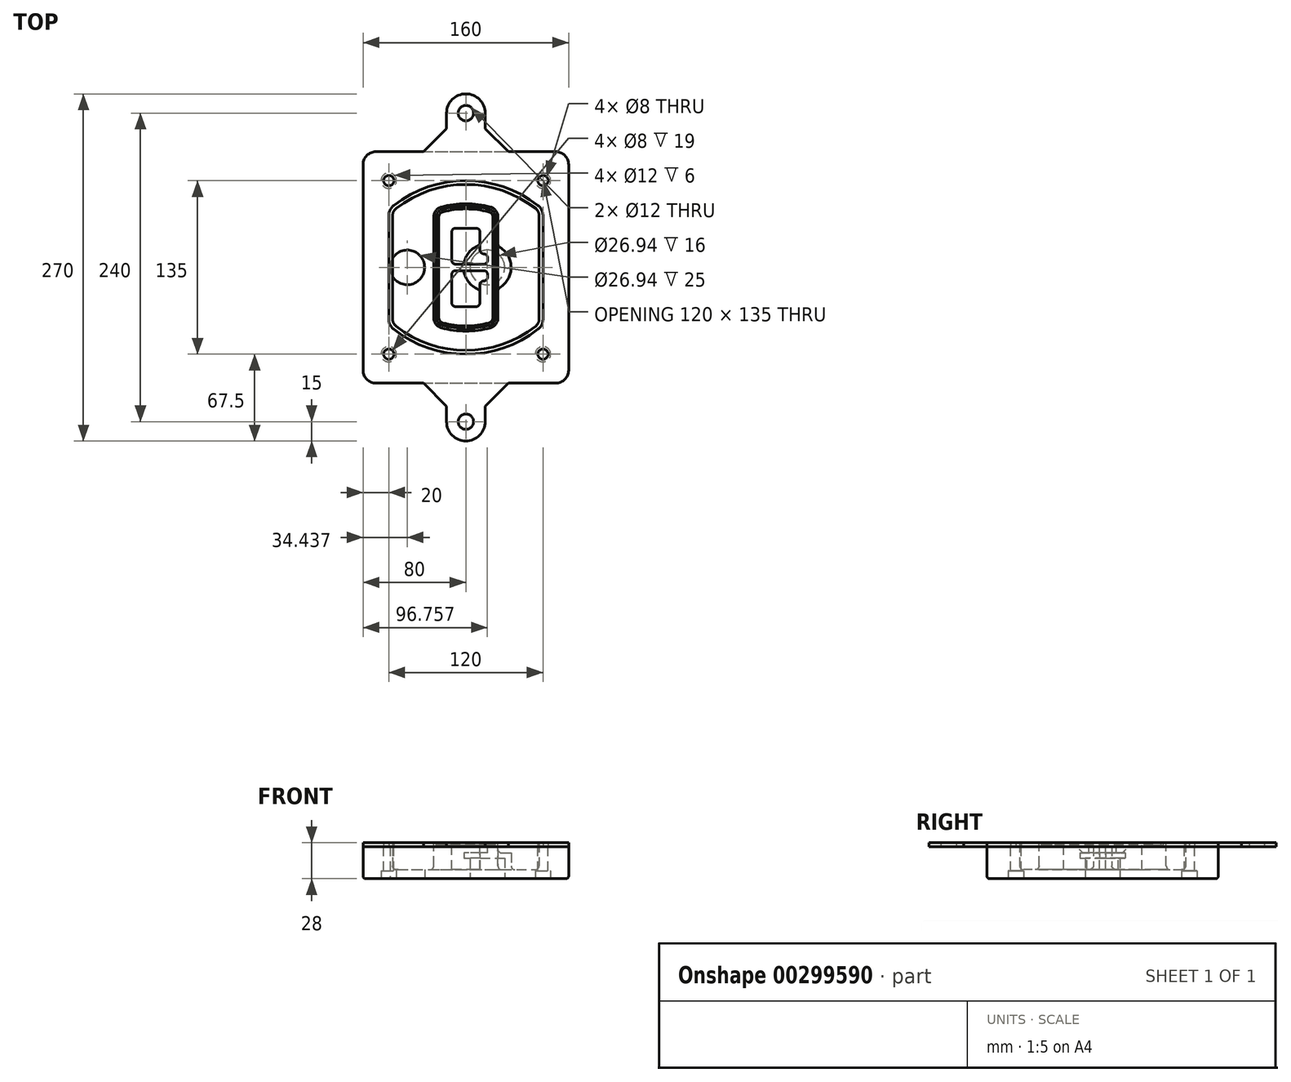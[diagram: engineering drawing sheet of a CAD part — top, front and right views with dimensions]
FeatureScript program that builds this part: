
annotation { "Feature Type Name" : "Feature", "Feature Type Description" : "" }
export const myFeature = defineFeature(function(context is Context, id is Id, definition is map)
    precondition{}
    {
        {
            var Q0;
            Q0=qCreatedBy(makeId("Top.planeOp"),FACE);
            var sketch = newSketch(context, id + "F0", { "sketchPlane" : qUnion([Q0])});
            skPoint(sketch, "E0.rect.middle", {"position": v(0, 0) * mm});
            skLineSegment(sketch, "E1.bottom", {"start": v(-70, -90) * mm, "end": v(70, -90) * mm});
            skLineSegment(sketch, "E1.top", {"start": v(-70, 90) * mm, "end": v(70, 90) * mm});
            skLineSegment(sketch, "E1.left", {"start": v(-80, -80) * mm, "end": v(-80, 80) * mm});
            skLineSegment(sketch, "E1.right", {"start": v(80, -80) * mm, "end": v(80, 80) * mm});
            skLineSegment(sketch, "E2", {"start": v(-80, 90) * mm, "end": v(80, -90) * mm, "construction": true});
            skLineSegment(sketch, "E3", {"start": v(80, 90) * mm, "end": v(-80, -90) * mm, "construction": true});
            skCircle(sketch, "E4", {"center": v(-60, 67.5) * mm, "radius": 4 * mm});
            skCircle(sketch, "E5", {"center": v(60, 67.5) * mm, "radius": 4 * mm});
            skCircle(sketch, "E6", {"center": v(60, -67.5) * mm, "radius": 4 * mm});
            skCircle(sketch, "E7", {"center": v(-60, -67.5) * mm, "radius": 4 * mm});
            skLineSegment(sketch, "E8", {"start": v(-60, 67.5) * mm, "end": v(60, 67.5) * mm, "construction": true});
            skLineSegment(sketch, "E9", {"start": v(60, 67.5) * mm, "end": v(60, -67.5) * mm, "construction": true});
            skLineSegment(sketch, "E10", {"start": v(60, -67.5) * mm, "end": v(-60, -67.5) * mm, "construction": true});
            skLineSegment(sketch, "E11", {"start": v(-60, -67.5) * mm, "end": v(-60, 67.5) * mm, "construction": true});
            skLineSegment(sketch, "E12", {"start": v(-60, 40.3) * mm, "end": v(-60, -40.3) * mm});
            skLineSegment(sketch, "E13", {"start": v(60, 40.3) * mm, "end": v(60, -40.3) * mm});
            skArc(sketch, "E14", {"start": v(56.15, 48.18) * mm, "mid": v(0, 67.5) * mm, "end": v(-56.15, 48.18) * mm});
            skArc(sketch, "E15", {"start": v(-56.15, -48.18) * mm, "mid": v(0, -67.5) * mm, "end": v(56.15, -48.18) * mm});
            skLineSegment(sketch, "E16", {"start": v(-60, 0) * mm, "end": v(60, 0) * mm, "construction": true});
            skPoint(sketch, "E17.visualSharp", {"position": v(-60, -45) * mm});
            skArc(sketch, "E17.filletArc", {"start": v(-60, -40.3) * mm, "mid": v(-58.99, -44.68) * mm, "end": v(-56.15, -48.18) * mm});
            skPoint(sketch, "E18.visualSharp", {"position": v(-60, 45) * mm});
            skArc(sketch, "E18.filletArc", {"start": v(-56.15, 48.18) * mm, "mid": v(-58.99, 44.68) * mm, "end": v(-60, 40.3) * mm});
            skPoint(sketch, "E19.visualSharp", {"position": v(60, 45) * mm});
            skArc(sketch, "E19.filletArc", {"start": v(60, 40.3) * mm, "mid": v(58.99, 44.68) * mm, "end": v(56.15, 48.18) * mm});
            skPoint(sketch, "E20.visualSharp", {"position": v(60, -45) * mm});
            skArc(sketch, "E20.filletArc", {"start": v(56.15, -48.18) * mm, "mid": v(58.99, -44.68) * mm, "end": v(60, -40.3) * mm});
            skPoint(sketch, "E21.visualSharp", {"position": v(-80, 90) * mm});
            skArc(sketch, "E21.filletArc", {"start": v(-70, 90) * mm, "mid": v(-77.07, 87.07) * mm, "end": v(-80, 80) * mm});
            skPoint(sketch, "E22.visualSharp", {"position": v(80, 90) * mm});
            skArc(sketch, "E22.filletArc", {"start": v(80, 80) * mm, "mid": v(77.07, 87.07) * mm, "end": v(70, 90) * mm});
            skPoint(sketch, "E23.visualSharp", {"position": v(80, -90) * mm});
            skArc(sketch, "E23.filletArc", {"start": v(70, -90) * mm, "mid": v(77.07, -87.07) * mm, "end": v(80, -80) * mm});
            skPoint(sketch, "E24.visualSharp", {"position": v(-80, -90) * mm});
            skArc(sketch, "E24.filletArc", {"start": v(-80, -80) * mm, "mid": v(-77.07, -87.07) * mm, "end": v(-70, -90) * mm});
            skArc(sketch, "E25.0", {"start": v(57, 40.3) * mm, "mid": v(56.3, 43.36) * mm, "end": v(54.3, 45.81) * mm});
            skLineSegment(sketch, "E25.1", {"start": v(57, 40.3) * mm, "end": v(57, -40.3) * mm});
            skArc(sketch, "E25.2", {"start": v(54.3, -45.81) * mm, "mid": v(56.3, -43.36) * mm, "end": v(57, -40.3) * mm});
            skArc(sketch, "E25.3", {"start": v(-54.3, -45.81) * mm, "mid": v(0, -64.5) * mm, "end": v(54.3, -45.81) * mm});
            skArc(sketch, "E25.4", {"start": v(-57, -40.3) * mm, "mid": v(-56.3, -43.36) * mm, "end": v(-54.3, -45.81) * mm});
            skArc(sketch, "E25.5", {"start": v(54.3, 45.81) * mm, "mid": v(0, 64.5) * mm, "end": v(-54.3, 45.81) * mm});
            skLineSegment(sketch, "E25.6", {"start": v(-57, 40.3) * mm, "end": v(-57, -40.3) * mm});
            skArc(sketch, "E25.7", {"start": v(-54.3, 45.81) * mm, "mid": v(-56.3, 43.36) * mm, "end": v(-57, 40.3) * mm});
            skArc(sketch, "E26.0", {"start": v(-58.62, 51.33) * mm, "mid": v(-62.58, 46.43) * mm, "end": v(-64, 40.3) * mm});
            skArc(sketch, "E26.1", {"start": v(58.62, 51.33) * mm, "mid": v(0, 71.5) * mm, "end": v(-58.62, 51.33) * mm});
            skArc(sketch, "E26.2", {"start": v(64, 40.3) * mm, "mid": v(62.58, 46.43) * mm, "end": v(58.62, 51.33) * mm});
            skLineSegment(sketch, "E26.3", {"start": v(64, 40.3) * mm, "end": v(64, -40.3) * mm});
            skArc(sketch, "E26.4", {"start": v(58.62, -51.33) * mm, "mid": v(62.58, -46.43) * mm, "end": v(64, -40.3) * mm});
            skLineSegment(sketch, "E26.5", {"start": v(-64, 40.3) * mm, "end": v(-64, -40.3) * mm});
            skArc(sketch, "E26.6", {"start": v(-58.62, -51.33) * mm, "mid": v(0, -71.5) * mm, "end": v(58.62, -51.33) * mm});
            skArc(sketch, "E26.7", {"start": v(-64, -40.3) * mm, "mid": v(-62.58, -46.43) * mm, "end": v(-58.62, -51.33) * mm});
            skSolve(sketch);
        }
        {
            var Q0;
            Q0=makeQuery(id+"F0.imprint","IMPRINT",FACE,{"disambiguationData":[TD([[makeQuery(id+"F0.imprint","IMPRINT",EDGE,{"derivedFrom":sQuery(id+"F0.wireOp",EDGE,"E1.bottom")}),1.0]])]});
            var Q1;
            Q1=makeQuery(id+"F0.imprint","IMPRINT",FACE,{"disambiguationData":[TD([[makeQuery(id+"F0.imprint","IMPRINT",EDGE,{"derivedFrom":sQuery(id+"F0.wireOp",EDGE,"E12")}),1.0]])]});
            var Q2;
            Q2=makeQuery(id+"F0.imprint","IMPRINT",FACE,{"disambiguationData":[TD([[makeQuery(id+"F0.imprint","IMPRINT",EDGE,{"derivedFrom":sQuery(id+"F0.wireOp",EDGE,"E25.0")}),1.0]])]});
            var Q3;
            Q3=makeQuery(id+"F0.imprint","IMPRINT",FACE,{"disambiguationData":[TD([[makeQuery(id+"F0.imprint","IMPRINT",EDGE,{"derivedFrom":sQuery(id+"F0.wireOp",EDGE,"E12")}),-1.0]])]});
            extrude(context, id + "F1", {"entities" : qUnion([Q0, Q1, Q2, Q3]), "oppositeDirection" : true, "depth" : 25 * mm});
        }
        {
            var Q0;
            Q0=makeQuery(id+"F0.imprint","IMPRINT",FACE,{"disambiguationData":[TD([[makeQuery(id+"F0.imprint","IMPRINT",EDGE,{"derivedFrom":sQuery(id+"F0.wireOp",EDGE,"E12")}),1.0]])]});
            extrude(context, id + "F2", {"entities" : qUnion([Q0]), "operationType" : NewBodyOperationType.ADD, "depth" : 3 * mm});
        }
        {
            var Q0;
            Q0=makeQuery(id+"F0.imprint","IMPRINT",FACE,{"disambiguationData":[TD([[makeQuery(id+"F0.imprint","IMPRINT",EDGE,{"derivedFrom":sQuery(id+"F0.wireOp",EDGE,"E25.0")}),1.0]])]});
            extrude(context, id + "F3", {"entities" : qUnion([Q0]), "operationType" : NewBodyOperationType.REMOVE, "oppositeDirection" : true, "depth" : 18 * mm});
        }
        {
            var Q0;
            Q0=makeQuery(id+"F2.opExtrude","CAP_FACE",FACE,{"disambiguationData":[OSD([sQuery(id+"F0.wireOp",EDGE,"E12"),sQuery(id+"F0.wireOp",EDGE,"E13"),sQuery(id+"F0.wireOp",EDGE,"E14"),sQuery(id+"F0.wireOp",EDGE,"E15"),sQuery(id+"F0.wireOp",EDGE,"E17.filletArc"),sQuery(id+"F0.wireOp",EDGE,"E18.filletArc"),sQuery(id+"F0.wireOp",EDGE,"E19.filletArc"),sQuery(id+"F0.wireOp",EDGE,"E20.filletArc"),sQuery(id+"F0.wireOp",EDGE,"E25.0"),sQuery(id+"F0.wireOp",EDGE,"E25.1"),sQuery(id+"F0.wireOp",EDGE,"E25.2"),sQuery(id+"F0.wireOp",EDGE,"E25.3"),sQuery(id+"F0.wireOp",EDGE,"E25.4"),sQuery(id+"F0.wireOp",EDGE,"E25.5"),sQuery(id+"F0.wireOp",EDGE,"E25.6"),sQuery(id+"F0.wireOp",EDGE,"E25.7")])],"isStart":false});
            var sketch = newSketch(context, id + "F4", { "sketchPlane" : qUnion([Q0])});
            skArc(sketch, "E27.0", {"start": v(-19.08, -46.97) * mm, "mid": v(0, -49.5) * mm, "end": v(19.08, -46.97) * mm});
            skArc(sketch, "E28.0", {"start": v(19.08, 46.97) * mm, "mid": v(0, 49.5) * mm, "end": v(-19.08, 46.97) * mm});
            skLineSegment(sketch, "E29", {"start": v(-25, 39.25) * mm, "end": v(-25, -39.25) * mm});
            skLineSegment(sketch, "E30", {"start": v(25, 39.25) * mm, "end": v(25, -39.25) * mm});
            skLineSegment(sketch, "E31", {"start": v(-25, 45.1) * mm, "end": v(25, 45.1) * mm, "construction": true});
            skLineSegment(sketch, "E32", {"start": v(-25, -45.1) * mm, "end": v(25, -45.1) * mm, "construction": true});
            skPoint(sketch, "E33.visualSharp", {"position": v(-25, 45.1) * mm});
            skArc(sketch, "E33.filletArc", {"start": v(-19.08, 46.97) * mm, "mid": v(-23.35, 44.11) * mm, "end": v(-25, 39.25) * mm});
            skPoint(sketch, "E34.visualSharp", {"position": v(25, 45.1) * mm});
            skArc(sketch, "E34.filletArc", {"start": v(25, 39.25) * mm, "mid": v(23.35, 44.11) * mm, "end": v(19.08, 46.97) * mm});
            skPoint(sketch, "E35.visualSharp", {"position": v(25, -45.1) * mm});
            skArc(sketch, "E35.filletArc", {"start": v(19.08, -46.97) * mm, "mid": v(23.35, -44.11) * mm, "end": v(25, -39.25) * mm});
            skPoint(sketch, "E36.visualSharp", {"position": v(-25, -45.1) * mm});
            skArc(sketch, "E36.filletArc", {"start": v(-25, -39.25) * mm, "mid": v(-23.35, -44.11) * mm, "end": v(-19.08, -46.97) * mm});
            skArc(sketch, "E37.0", {"start": v(54.3, 45.81) * mm, "mid": v(0, 64.5) * mm, "end": v(-54.3, 45.81) * mm});
            skArc(sketch, "E37.1", {"start": v(-54.3, 45.81) * mm, "mid": v(-56.3, 43.36) * mm, "end": v(-57, 40.3) * mm});
            skLineSegment(sketch, "E37.2", {"start": v(-57, 40.3) * mm, "end": v(-57, -40.3) * mm});
            skArc(sketch, "E37.3", {"start": v(-57, -40.3) * mm, "mid": v(-56.3, -43.36) * mm, "end": v(-54.3, -45.81) * mm});
            skArc(sketch, "E37.4", {"start": v(-54.3, -45.81) * mm, "mid": v(0, -64.5) * mm, "end": v(54.3, -45.81) * mm});
            skArc(sketch, "E37.5", {"start": v(54.3, -45.81) * mm, "mid": v(56.3, -43.36) * mm, "end": v(57, -40.3) * mm});
            skLineSegment(sketch, "E37.6", {"start": v(57, 40.3) * mm, "end": v(57, -40.3) * mm});
            skArc(sketch, "E37.7", {"start": v(57, 40.3) * mm, "mid": v(56.3, 43.36) * mm, "end": v(54.3, 45.81) * mm});
            skLineSegment(sketch, "E38.0", {"start": v(23, 39.25) * mm, "end": v(23, -39.25) * mm});
            skArc(sketch, "E38.1", {"start": v(18.56, -45.04) * mm, "mid": v(21.76, -42.9) * mm, "end": v(23, -39.25) * mm});
            skArc(sketch, "E38.2", {"start": v(-18.56, -45.04) * mm, "mid": v(0, -47.5) * mm, "end": v(18.56, -45.04) * mm});
            skArc(sketch, "E38.3", {"start": v(-23, -39.25) * mm, "mid": v(-21.76, -42.9) * mm, "end": v(-18.56, -45.04) * mm});
            skLineSegment(sketch, "E38.4", {"start": v(-23, 39.25) * mm, "end": v(-23, -39.25) * mm});
            skArc(sketch, "E38.5", {"start": v(23, 39.25) * mm, "mid": v(21.76, 42.9) * mm, "end": v(18.56, 45.04) * mm});
            skArc(sketch, "E38.6", {"start": v(-18.56, 45.04) * mm, "mid": v(-21.76, 42.9) * mm, "end": v(-23, 39.25) * mm});
            skArc(sketch, "E38.7", {"start": v(18.56, 45.04) * mm, "mid": v(0, 47.5) * mm, "end": v(-18.56, 45.04) * mm});
            skArc(sketch, "E39.0", {"start": v(21, 39.25) * mm, "mid": v(20.18, 41.68) * mm, "end": v(18.04, 43.1) * mm});
            skLineSegment(sketch, "E39.1", {"start": v(21, 39.25) * mm, "end": v(21, -39.25) * mm});
            skArc(sketch, "E39.2", {"start": v(18.04, -43.1) * mm, "mid": v(20.18, -41.68) * mm, "end": v(21, -39.25) * mm});
            skArc(sketch, "E39.3", {"start": v(-18.04, -43.1) * mm, "mid": v(0, -45.5) * mm, "end": v(18.04, -43.1) * mm});
            skArc(sketch, "E39.4", {"start": v(-21, -39.25) * mm, "mid": v(-20.18, -41.68) * mm, "end": v(-18.04, -43.1) * mm});
            skArc(sketch, "E39.5", {"start": v(18.04, 43.1) * mm, "mid": v(0, 45.5) * mm, "end": v(-18.04, 43.1) * mm});
            skLineSegment(sketch, "E39.6", {"start": v(-21, 39.25) * mm, "end": v(-21, -39.25) * mm});
            skArc(sketch, "E39.7", {"start": v(-18.04, 43.1) * mm, "mid": v(-20.18, 41.68) * mm, "end": v(-21, 39.25) * mm});
            skLineSegment(sketch, "E40", {"start": v(-25, 0) * mm, "end": v(25, 0) * mm, "construction": true});
            skLineSegment(sketch, "E41", {"start": v(-11, 5.5) * mm, "end": v(-11, 27.5) * mm});
            skLineSegment(sketch, "E42", {"start": v(-8, 30.5) * mm, "end": v(8, 30.5) * mm});
            skLineSegment(sketch, "E43", {"start": v(11, 27.5) * mm, "end": v(11, 13.5) * mm});
            skLineSegment(sketch, "E44", {"start": v(14, 10.5) * mm, "end": v(14, 10.5) * mm});
            skLineSegment(sketch, "E45", {"start": v(17, 7.5) * mm, "end": v(17, 5.5) * mm});
            skLineSegment(sketch, "E46", {"start": v(14, 2.5) * mm, "end": v(-8, 2.5) * mm});
            skPoint(sketch, "E47.visualSharp", {"position": v(-11, 30.5) * mm});
            skArc(sketch, "E47.filletArc", {"start": v(-8, 30.5) * mm, "mid": v(-10.12, 29.62) * mm, "end": v(-11, 27.5) * mm});
            skPoint(sketch, "E48.visualSharp", {"position": v(11, 30.5) * mm});
            skArc(sketch, "E48.filletArc", {"start": v(11, 27.5) * mm, "mid": v(10.12, 29.62) * mm, "end": v(8, 30.5) * mm});
            skPoint(sketch, "E49.visualSharp", {"position": v(11, 10.5) * mm});
            skArc(sketch, "E49.filletArc", {"start": v(11, 13.5) * mm, "mid": v(11.88, 11.38) * mm, "end": v(14, 10.5) * mm});
            skPoint(sketch, "E50.visualSharp", {"position": v(17, 10.5) * mm});
            skArc(sketch, "E50.filletArc", {"start": v(17, 7.5) * mm, "mid": v(16.12, 9.62) * mm, "end": v(14, 10.5) * mm});
            skPoint(sketch, "E51.visualSharp", {"position": v(17, 2.5) * mm});
            skArc(sketch, "E51.filletArc", {"start": v(14, 2.5) * mm, "mid": v(16.12, 3.38) * mm, "end": v(17, 5.5) * mm});
            skPoint(sketch, "E52.visualSharp", {"position": v(-11, 2.5) * mm});
            skArc(sketch, "E52.filletArc", {"start": v(-11, 5.5) * mm, "mid": v(-10.12, 3.38) * mm, "end": v(-8, 2.5) * mm});
            skLineSegment(sketch, "E53.0.MirrorCS", {"start": v(14, -2.5) * mm, "end": v(-8, -2.5) * mm});
            skArc(sketch, "E54.0.MirrorCS", {"start": v(-11, -5.5) * mm, "mid": v(-10.12, -3.38) * mm, "end": v(-8, -2.5) * mm});
            skLineSegment(sketch, "E55.0.MirrorCS", {"start": v(-11, -5.5) * mm, "end": v(-11, -27.5) * mm});
            skArc(sketch, "E56.0.MirrorCS", {"start": v(-8, -30.5) * mm, "mid": v(-10.12, -29.62) * mm, "end": v(-11, -27.5) * mm});
            skLineSegment(sketch, "E57.0.MirrorCS", {"start": v(-8, -30.5) * mm, "end": v(8, -30.5) * mm});
            skArc(sketch, "E58.0.MirrorCS", {"start": v(11, -27.5) * mm, "mid": v(10.12, -29.62) * mm, "end": v(8, -30.5) * mm});
            skLineSegment(sketch, "E59.0.MirrorCS", {"start": v(11, -27.5) * mm, "end": v(11, -13.5) * mm});
            skArc(sketch, "E60.0.MirrorCS", {"start": v(11, -13.5) * mm, "mid": v(11.88, -11.38) * mm, "end": v(14, -10.5) * mm});
            skArc(sketch, "E61.0.MirrorCS", {"start": v(17, -7.5) * mm, "mid": v(16.12, -9.62) * mm, "end": v(14, -10.5) * mm});
            skLineSegment(sketch, "E62.0.MirrorCS", {"start": v(17, -7.5) * mm, "end": v(17, -5.5) * mm});
            skArc(sketch, "E63.0.MirrorCS", {"start": v(14, -2.5) * mm, "mid": v(16.12, -3.38) * mm, "end": v(17, -5.5) * mm});
            skSolve(sketch);
        }
        {
            var Q0;
            Q0=makeQuery(id+"F4.imprint","IMPRINT",FACE,{"disambiguationData":[TD([[makeQuery(id+"F4.imprint","IMPRINT",EDGE,{"derivedFrom":sQuery(id+"F4.wireOp",EDGE,"E27.0")}),1.0]])]});
            var Q1;
            Q1=makeQuery(id+"F4.imprint","IMPRINT",FACE,{"disambiguationData":[TD([[makeQuery(id+"F4.imprint","IMPRINT",EDGE,{"derivedFrom":sQuery(id+"F4.wireOp",EDGE,"E38.0")}),-1.0]])]});
            var Q2;
            Q2=makeQuery(id+"F4.imprint","IMPRINT",FACE,{"disambiguationData":[TD([[makeQuery(id+"F4.imprint","IMPRINT",EDGE,{"derivedFrom":sQuery(id+"F4.wireOp",EDGE,"E39.0")}),1.0]])]});
            extrude(context, id + "F5", {"entities" : qUnion([Q0, Q1, Q2]), "operationType" : NewBodyOperationType.ADD, "endBound" : BoundingType.UP_TO_NEXT, "oppositeDirection" : true, "depth" : 25 * mm});
        }
        {
            var Q0;
            Q0=makeQuery(id+"F4.imprint","IMPRINT",FACE,{"disambiguationData":[TD([[makeQuery(id+"F4.imprint","IMPRINT",EDGE,{"derivedFrom":sQuery(id+"F4.wireOp",EDGE,"E38.0")}),-1.0]])]});
            extrude(context, id + "F6", {"entities" : qUnion([Q0]), "operationType" : NewBodyOperationType.REMOVE, "oppositeDirection" : true, "depth" : 2 * mm});
        }
        {
            var Q0;
            Q0=makeQuery(id+"F1.opExtrude","CAP_FACE",FACE,{"disambiguationData":[OSD([sQuery(id+"F0.wireOp",EDGE,"E1.bottom"),sQuery(id+"F0.wireOp",EDGE,"E1.top"),sQuery(id+"F0.wireOp",EDGE,"E1.left"),sQuery(id+"F0.wireOp",EDGE,"E1.right"),sQuery(id+"F0.wireOp",EDGE,"E4"),sQuery(id+"F0.wireOp",EDGE,"E5"),sQuery(id+"F0.wireOp",EDGE,"E6"),sQuery(id+"F0.wireOp",EDGE,"E7"),sQuery(id+"F0.wireOp",EDGE,"E21.filletArc"),sQuery(id+"F0.wireOp",EDGE,"E22.filletArc"),sQuery(id+"F0.wireOp",EDGE,"E23.filletArc"),sQuery(id+"F0.wireOp",EDGE,"E24.filletArc")])],"isStart":false});
            var sketch = newSketch(context, id + "F7", { "sketchPlane" : qUnion([Q0])});
            skCircle(sketch, "E64", {"center": v(16.76, 0) * mm, "radius": 13.47 * mm});
            skCircle(sketch, "E65", {"center": v(-45.56, 0) * mm, "radius": 13.47 * mm});
            skLineSegment(sketch, "E66", {"start": v(80, 0) * mm, "end": v(-80, 0) * mm});
            skCircle(sketch, "E67", {"center": v(16.76, 0) * mm, "radius": 18.47 * mm});
            skCircle(sketch, "E68", {"center": v(60, -67.5) * mm, "radius": 6 * mm});
            skCircle(sketch, "E69", {"center": v(-60, -67.5) * mm, "radius": 6 * mm});
            skCircle(sketch, "E70", {"center": v(-60, 67.5) * mm, "radius": 6 * mm});
            skCircle(sketch, "E71", {"center": v(60, 67.5) * mm, "radius": 6 * mm});
            skSolve(sketch);
        }
        {
            var Q0;
            {var subQ1=sQuery(id+"F7.wireOp",EDGE,"E66");var subQ4=sQuery(id+"F7.wireOp",EDGE,"E64");var subQ6=makeQuery(id+"F7.imprint","INTERSECT",VERTEX,{"disambiguationData":[OD(0.0)],"derivedFrom":[subQ4,subQ1]});Q0=makeQuery(id+"F7.imprint","IMPRINT",FACE,{"disambiguationData":[TD([[makeQuery(id+"F7.imprint","IMPRINT",EDGE,{"disambiguationData":[TD([[subQ6,-1.0]])],"derivedFrom":subQ4}),-1.0]])]});}
            var Q1;
            {var subQ0=sQuery(id+"F7.wireOp",EDGE,"E66");var subQ1=sQuery(id+"F7.wireOp",EDGE,"E64");var subQ3=makeQuery(id+"F7.imprint","INTERSECT",VERTEX,{"disambiguationData":[OD(0.0)],"derivedFrom":[subQ1,subQ0]});Q1=makeQuery(id+"F7.imprint","IMPRINT",FACE,{"disambiguationData":[TD([[makeQuery(id+"F7.imprint","IMPRINT",EDGE,{"disambiguationData":[TD([[subQ3,-1.0]])],"derivedFrom":subQ1}),1.0]])]});}
            var Q2;
            {var subQ0=sQuery(id+"F7.wireOp",EDGE,"E66");var subQ1=sQuery(id+"F7.wireOp",EDGE,"E64");var subQ3=makeQuery(id+"F7.imprint","INTERSECT",VERTEX,{"disambiguationData":[OD(0.0)],"derivedFrom":[subQ1,subQ0]});Q2=makeQuery(id+"F7.imprint","IMPRINT",FACE,{"disambiguationData":[TD([[makeQuery(id+"F7.imprint","IMPRINT",EDGE,{"disambiguationData":[TD([[subQ3,1.0]])],"derivedFrom":subQ1}),1.0]])]});}
            var Q3;
            {var subQ1=sQuery(id+"F7.wireOp",EDGE,"E66");var subQ4=sQuery(id+"F7.wireOp",EDGE,"E64");var subQ6=makeQuery(id+"F7.imprint","INTERSECT",VERTEX,{"disambiguationData":[OD(0.0)],"derivedFrom":[subQ4,subQ1]});Q3=makeQuery(id+"F7.imprint","IMPRINT",FACE,{"disambiguationData":[TD([[makeQuery(id+"F7.imprint","IMPRINT",EDGE,{"disambiguationData":[TD([[subQ6,1.0]])],"derivedFrom":subQ4}),-1.0]])]});}
            extrude(context, id + "F8", {"entities" : qUnion([Q0, Q1, Q2, Q3]), "operationType" : NewBodyOperationType.ADD, "oppositeDirection" : true, "depth" : 20 * mm});
        }
        {
            var Q0;
            {var subQ0=sQuery(id+"F7.wireOp",EDGE,"E66");var subQ1=sQuery(id+"F7.wireOp",EDGE,"E64");var subQ3=makeQuery(id+"F7.imprint","INTERSECT",VERTEX,{"disambiguationData":[OD(0.0)],"derivedFrom":[subQ1,subQ0]});Q0=makeQuery(id+"F7.imprint","IMPRINT",FACE,{"disambiguationData":[TD([[makeQuery(id+"F7.imprint","IMPRINT",EDGE,{"disambiguationData":[TD([[subQ3,-1.0]])],"derivedFrom":subQ1}),1.0]])]});}
            var Q1;
            {var subQ0=sQuery(id+"F7.wireOp",EDGE,"E66");var subQ1=sQuery(id+"F7.wireOp",EDGE,"E64");var subQ3=makeQuery(id+"F7.imprint","INTERSECT",VERTEX,{"disambiguationData":[OD(0.0)],"derivedFrom":[subQ1,subQ0]});Q1=makeQuery(id+"F7.imprint","IMPRINT",FACE,{"disambiguationData":[TD([[makeQuery(id+"F7.imprint","IMPRINT",EDGE,{"disambiguationData":[TD([[subQ3,1.0]])],"derivedFrom":subQ1}),1.0]])]});}
            extrude(context, id + "F9", {"entities" : qUnion([Q0, Q1]), "operationType" : NewBodyOperationType.REMOVE, "oppositeDirection" : true, "depth" : 16 * mm});
        }
        {
            var Q0;
            {var subQ0=sQuery(id+"F7.wireOp",EDGE,"E66");var subQ1=sQuery(id+"F7.wireOp",EDGE,"E65");var subQ3=makeQuery(id+"F7.imprint","INTERSECT",VERTEX,{"disambiguationData":[OD(0.0)],"derivedFrom":[subQ1,subQ0]});Q0=makeQuery(id+"F7.imprint","IMPRINT",FACE,{"disambiguationData":[TD([[makeQuery(id+"F7.imprint","IMPRINT",EDGE,{"disambiguationData":[TD([[subQ3,-1.0]])],"derivedFrom":subQ1}),1.0]])]});}
            var Q1;
            {var subQ0=sQuery(id+"F7.wireOp",EDGE,"E66");var subQ1=sQuery(id+"F7.wireOp",EDGE,"E65");var subQ3=makeQuery(id+"F7.imprint","INTERSECT",VERTEX,{"disambiguationData":[OD(0.0)],"derivedFrom":[subQ1,subQ0]});Q1=makeQuery(id+"F7.imprint","IMPRINT",FACE,{"disambiguationData":[TD([[makeQuery(id+"F7.imprint","IMPRINT",EDGE,{"disambiguationData":[TD([[subQ3,1.0]])],"derivedFrom":subQ1}),1.0]])]});}
            extrude(context, id + "F10", {"entities" : qUnion([Q0, Q1]), "operationType" : NewBodyOperationType.REMOVE, "oppositeDirection" : true, "depth" : 25 * mm});
        }
        {
            var Q0;
            Q0=makeQuery(id+"F7.imprint","IMPRINT",FACE,{"disambiguationData":[TD([[makeQuery(id+"F7.imprint","IMPRINT",EDGE,{"derivedFrom":sQuery(id+"F7.wireOp",EDGE,"E68")}),1.0]])]});
            var Q1;
            Q1=makeQuery(id+"F7.imprint","IMPRINT",FACE,{"disambiguationData":[TD([[makeQuery(id+"F7.imprint","IMPRINT",EDGE,{"derivedFrom":makeQuery(id+"F1.opExtrude","CAP_EDGE",EDGE,{"disambiguationData":[OSD([sQuery(id+"F0.wireOp",EDGE,"E5")])],"isStart":false})}),-1.0]])]});
            var Q2;
            Q2=makeQuery(id+"F7.imprint","IMPRINT",FACE,{"disambiguationData":[TD([[makeQuery(id+"F7.imprint","IMPRINT",EDGE,{"derivedFrom":sQuery(id+"F7.wireOp",EDGE,"E69")}),1.0]])]});
            var Q3;
            Q3=makeQuery(id+"F7.imprint","IMPRINT",FACE,{"disambiguationData":[TD([[makeQuery(id+"F7.imprint","IMPRINT",EDGE,{"derivedFrom":makeQuery(id+"F1.opExtrude","CAP_EDGE",EDGE,{"disambiguationData":[OSD([sQuery(id+"F0.wireOp",EDGE,"E4")])],"isStart":false})}),-1.0]])]});
            var Q4;
            Q4=makeQuery(id+"F7.imprint","IMPRINT",FACE,{"disambiguationData":[TD([[makeQuery(id+"F7.imprint","IMPRINT",EDGE,{"derivedFrom":sQuery(id+"F7.wireOp",EDGE,"E70")}),1.0]])]});
            var Q5;
            Q5=makeQuery(id+"F7.imprint","IMPRINT",FACE,{"disambiguationData":[TD([[makeQuery(id+"F7.imprint","IMPRINT",EDGE,{"derivedFrom":makeQuery(id+"F1.opExtrude","CAP_EDGE",EDGE,{"disambiguationData":[OSD([sQuery(id+"F0.wireOp",EDGE,"E7")])],"isStart":false})}),-1.0]])]});
            var Q6;
            Q6=makeQuery(id+"F7.imprint","IMPRINT",FACE,{"disambiguationData":[TD([[makeQuery(id+"F7.imprint","IMPRINT",EDGE,{"derivedFrom":sQuery(id+"F7.wireOp",EDGE,"E71")}),1.0]])]});
            var Q7;
            Q7=makeQuery(id+"F7.imprint","IMPRINT",FACE,{"disambiguationData":[TD([[makeQuery(id+"F7.imprint","IMPRINT",EDGE,{"derivedFrom":makeQuery(id+"F1.opExtrude","CAP_EDGE",EDGE,{"disambiguationData":[OSD([sQuery(id+"F0.wireOp",EDGE,"E6")])],"isStart":false})}),-1.0]])]});
            extrude(context, id + "F11", {"entities" : qUnion([Q0, Q1, Q2, Q3, Q4, Q5, Q6, Q7]), "operationType" : NewBodyOperationType.REMOVE, "oppositeDirection" : true, "depth" : 6 * mm});
        }
        {
            var Q0;
            Q0=makeQuery(id+"F9.boolean.opBoolean","COPY",FACE,{"derivedFrom":makeQuery(id+"F9.opExtrude","CAP_FACE",FACE,{"disambiguationData":[OSD([sQuery(id+"F7.wireOp",EDGE,"E64")])],"isStart":false})});
            var sketch = newSketch(context, id + "F12", { "sketchPlane" : qUnion([Q0])});
            skArc(sketch, "E72.0", {"start": v(11, 17.55) * mm, "mid": v(2.57, 11.82) * mm, "end": v(-1.54, 2.5) * mm});
            skArc(sketch, "E72.1", {"start": v(-1.54, -2.5) * mm, "mid": v(2.57, -11.82) * mm, "end": v(11, -17.55) * mm});
            skLineSegment(sketch, "E73", {"start": v(-1.54, -2.5) * mm, "end": v(14, -2.5) * mm});
            skLineSegment(sketch, "E74.0", {"start": v(14, 2.5) * mm, "end": v(-1.54, 2.5) * mm});
            skArc(sketch, "E74.1", {"start": v(14, 2.5) * mm, "mid": v(16.12, 3.38) * mm, "end": v(17, 5.5) * mm});
            skLineSegment(sketch, "E74.2", {"start": v(17, 7.5) * mm, "end": v(17, 5.5) * mm});
            skArc(sketch, "E74.3", {"start": v(17, 7.5) * mm, "mid": v(16.12, 9.62) * mm, "end": v(14, 10.5) * mm});
            skArc(sketch, "E74.4", {"start": v(11, 13.5) * mm, "mid": v(11.88, 11.38) * mm, "end": v(14, 10.5) * mm});
            skLineSegment(sketch, "E74.5", {"start": v(11, 17.55) * mm, "end": v(11, 13.5) * mm});
            skLineSegment(sketch, "E74.7", {"start": v(14, -2.5) * mm, "end": v(-1.54, -2.5) * mm});
            skArc(sketch, "E74.8", {"start": v(14, -2.5) * mm, "mid": v(16.12, -3.38) * mm, "end": v(17, -5.5) * mm});
            skLineSegment(sketch, "E74.9", {"start": v(17, -7.5) * mm, "end": v(17, -5.5) * mm});
            skArc(sketch, "E74.10", {"start": v(17, -7.5) * mm, "mid": v(16.12, -9.62) * mm, "end": v(14, -10.5) * mm});
            skArc(sketch, "E74.11", {"start": v(11, -13.5) * mm, "mid": v(11.88, -11.38) * mm, "end": v(14, -10.5) * mm});
            skLineSegment(sketch, "E74.12", {"start": v(11, -17.55) * mm, "end": v(11, -13.5) * mm});
            skPoint(sketch, "E75.orphan", {"position": v(11, -27.5) * mm});
            skPoint(sketch, "E76.orphan", {"position": v(-8, -2.5) * mm});
            skPoint(sketch, "E77.orphan", {"position": v(-8, 2.5) * mm});
            skPoint(sketch, "E78.orphan", {"position": v(11, 27.5) * mm});
            skSolve(sketch);
        }
        {
            var Q0;
            {var subQ7=sQuery(id+"F12.wireOp",EDGE,"E72.0");var subQ14=sQuery(id+"F12.wireOp",EDGE,"E72.1");var subQ16=sQuery(id+"F12.wireOp",EDGE,"E74.1");var subQ18=sQuery(id+"F12.wireOp",EDGE,"E74.8");Q0=qUnion([makeQuery(id+"F12.imprint","IMPRINT",FACE,{"disambiguationData":[TD([[makeQuery(id+"F12.imprint","IMPRINT",EDGE,{"derivedFrom":subQ7}),1.0]])]}),makeQuery(id+"F12.imprint","IMPRINT",FACE,{"disambiguationData":[TD([[makeQuery(id+"F12.imprint","IMPRINT",EDGE,{"derivedFrom":subQ14}),1.0]])]}),makeQuery(id+"F12.imprint","IMPRINT",FACE,{"disambiguationData":[TD([[makeQuery(id+"F12.imprint","IMPRINT",EDGE,{"derivedFrom":subQ16}),1.0]])]}),makeQuery(id+"F12.imprint","IMPRINT",FACE,{"disambiguationData":[TD([[makeQuery(id+"F12.imprint","IMPRINT",EDGE,{"derivedFrom":subQ18}),-1.0]])]})]);}
            var Q1;
            Q1=makeQuery(id+"F5.boolean.opBoolean","SPLIT",FACE,{"disambiguationData":[TD([makeQuery(id+"F5.opExtrude","SWEPT_FACE",FACE,{"disambiguationData":[OSD([sQuery(id+"F4.wireOp",EDGE,"E41")])]})])],"derivedFrom":makeQuery(id+"F3.boolean.opBoolean","COPY",FACE,{"derivedFrom":makeQuery(id+"F3.opExtrude","CAP_FACE",FACE,{"disambiguationData":[OSD([sQuery(id+"F0.wireOp",EDGE,"E25.0"),sQuery(id+"F0.wireOp",EDGE,"E25.1"),sQuery(id+"F0.wireOp",EDGE,"E25.2"),sQuery(id+"F0.wireOp",EDGE,"E25.3"),sQuery(id+"F0.wireOp",EDGE,"E25.4"),sQuery(id+"F0.wireOp",EDGE,"E25.5"),sQuery(id+"F0.wireOp",EDGE,"E25.6"),sQuery(id+"F0.wireOp",EDGE,"E25.7")])],"isStart":false})})});
            extrude(context, id + "F13", {"entities" : qUnion([Q0]), "operationType" : NewBodyOperationType.REMOVE, "endBound" : BoundingType.UP_TO_SURFACE, "endBoundEntityFace" : qUnion([Q1]), "depth" : 25 * mm});
        }
        {
            var Q0;
            Q0=makeQuery(id+"F3.boolean.opBoolean","COPY",EDGE,{"derivedFrom":makeQuery(id+"F3.opExtrude","CAP_EDGE",EDGE,{"disambiguationData":[OSD([sQuery(id+"F0.wireOp",EDGE,"E25.6")])],"isStart":false})});
            var Q1;
            Q1=makeQuery(id+"F8.boolean.opBoolean","INTERSECT",EDGE,{"derivedFrom":[makeQuery(id+"F5.opExtrude","SWEPT_FACE",FACE,{"disambiguationData":[OSD([sQuery(id+"F4.wireOp",EDGE,"E30")])]}),makeQuery(id+"F8.opExtrude","CAP_FACE",FACE,{"disambiguationData":[OSD([sQuery(id+"F7.wireOp",EDGE,"E67")])],"isStart":false})]});
            var Q2;
            Q2=makeQuery(id+"F8.boolean.opBoolean","INTERSECT",EDGE,{"disambiguationData":[OD(1.0)],"derivedFrom":[makeQuery(id+"F5.opExtrude","SWEPT_FACE",FACE,{"disambiguationData":[OSD([sQuery(id+"F4.wireOp",EDGE,"E30")])]}),makeQuery(id+"F8.opExtrude","SWEPT_FACE",FACE,{"disambiguationData":[OSD([sQuery(id+"F7.wireOp",EDGE,"E67")])]})]});
            var Q3;
            {var subQ0=sQuery(id+"F4.wireOp",EDGE,"E30");Q3=makeQuery(id+"F8.boolean.opBoolean","SPLIT",EDGE,{"disambiguationData":[TD([makeQuery(id+"F5.opExtrude","SWEPT_FACE",FACE,{"disambiguationData":[OSD([sQuery(id+"F4.wireOp",EDGE,"E35.filletArc")])]})])],"derivedFrom":makeQuery(id+"F5.opExtrude","CAP_EDGE",EDGE,{"disambiguationData":[OSD([subQ0])],"isStart":false})});}
            var Q4;
            {var subQ0=sQuery(id+"F0.wireOp",EDGE,"E25.7");var subQ1=sQuery(id+"F0.wireOp",EDGE,"E25.1");var subQ2=sQuery(id+"F0.wireOp",EDGE,"E25.6");var subQ3=sQuery(id+"F0.wireOp",EDGE,"E25.5");var subQ4=sQuery(id+"F0.wireOp",EDGE,"E25.4");var subQ5=sQuery(id+"F0.wireOp",EDGE,"E25.0");var subQ6=sQuery(id+"F0.wireOp",EDGE,"E25.2");var subQ7=sQuery(id+"F0.wireOp",EDGE,"E25.3");Q4=makeQuery(id+"F8.boolean.opBoolean","INTERSECT",EDGE,{"derivedFrom":[makeQuery(id+"F5.boolean.opBoolean","SPLIT",FACE,{"disambiguationData":[TD([makeQuery(id+"F2.opExtrude","SWEPT_FACE",FACE,{"disambiguationData":[OSD([subQ5])]})])],"derivedFrom":makeQuery(id+"F3.boolean.opBoolean","COPY",FACE,{"derivedFrom":makeQuery(id+"F3.opExtrude","CAP_FACE",FACE,{"disambiguationData":[OSD([subQ5,subQ1,subQ6,subQ7,subQ4,subQ3,subQ2,subQ0])],"isStart":false})})}),makeQuery(id+"F8.opExtrude","SWEPT_FACE",FACE,{"disambiguationData":[OSD([sQuery(id+"F7.wireOp",EDGE,"E67")])]})]});}
            var Q5;
            Q5=makeQuery(id+"F8.boolean.opBoolean","INTERSECT",EDGE,{"disambiguationData":[OD(0.0)],"derivedFrom":[makeQuery(id+"F5.opExtrude","SWEPT_FACE",FACE,{"disambiguationData":[OSD([sQuery(id+"F4.wireOp",EDGE,"E30")])]}),makeQuery(id+"F8.opExtrude","SWEPT_FACE",FACE,{"disambiguationData":[OSD([sQuery(id+"F7.wireOp",EDGE,"E67")])]})]});
            fillet(context, id + "F14", {"entities" : qUnion([Q0, Q1, Q2, Q3, Q4, Q5]), "radius" : 3 * mm, "tangentPropagation" : true, "allowEdgeOverflow" : false});
        }
        {
            var Q0;
            Q0=makeQuery(id+"F1.opExtrude","CAP_EDGE",EDGE,{"disambiguationData":[OSD([sQuery(id+"F0.wireOp",EDGE,"E1.bottom")])],"isStart":false});
            fillet(context, id + "F15", {"entities" : qUnion([Q0]), "radius" : 2 * mm, "tangentPropagation" : true, "allowEdgeOverflow" : false});
        }
        {
            var Q0;
            {var subQ0=sQuery(id+"F0.wireOp",EDGE,"E21.filletArc");var subQ1=sQuery(id+"F0.wireOp",EDGE,"E7");var subQ2=sQuery(id+"F0.wireOp",EDGE,"E6");var subQ3=sQuery(id+"F0.wireOp",EDGE,"E5");var subQ4=sQuery(id+"F0.wireOp",EDGE,"E4");var subQ5=sQuery(id+"F0.wireOp",EDGE,"E22.filletArc");var subQ6=sQuery(id+"F0.wireOp",EDGE,"E1.bottom");var subQ7=sQuery(id+"F0.wireOp",EDGE,"E1.right");var subQ8=sQuery(id+"F0.wireOp",EDGE,"E1.top");var subQ9=sQuery(id+"F0.wireOp",EDGE,"E1.left");var subQ10=sQuery(id+"F0.wireOp",EDGE,"E23.filletArc");var subQ11=sQuery(id+"F0.wireOp",EDGE,"E24.filletArc");Q0=makeQuery(id+"F2.boolean.opBoolean","SPLIT",FACE,{"disambiguationData":[TD([makeQuery(id+"F1.opExtrude","SWEPT_FACE",FACE,{"disambiguationData":[OSD([subQ6])]})])],"derivedFrom":makeQuery(id+"F1.opExtrude","CAP_FACE",FACE,{"disambiguationData":[OSD([subQ6,subQ8,subQ9,subQ7,subQ4,subQ3,subQ2,subQ1,subQ0,subQ5,subQ10,subQ11])],"isStart":true})});}
            var sketch = newSketch(context, id + "F16", { "sketchPlane" : qUnion([Q0])});
            skCircle(sketch, "E79", {"center": v(0, 120) * mm, "radius": 6 * mm});
            skArc(sketch, "E80", {"start": v(15, 120) * mm, "mid": v(0, 135) * mm, "end": v(-15, 120) * mm});
            skLineSegment(sketch, "E81", {"start": v(-15, 120) * mm, "end": v(-15, 108) * mm});
            skLineSegment(sketch, "E82", {"start": v(-15, 108) * mm, "end": v(-33, 90) * mm});
            skLineSegment(sketch, "E83", {"start": v(15, 120) * mm, "end": v(15, 108) * mm});
            skLineSegment(sketch, "E84", {"start": v(15, 108) * mm, "end": v(33, 90) * mm});
            skLineSegment(sketch, "E85", {"start": v(0, 120) * mm, "end": v(0, 90) * mm, "construction": true});
            skLineSegment(sketch, "E86", {"start": v(-33, 90) * mm, "end": v(33, 90) * mm});
            skLineSegment(sketch, "E87", {"start": v(-80, 0) * mm, "end": v(80, 0) * mm, "construction": true});
            skLineSegment(sketch, "E88.MirrorCS", {"start": v(15, -120) * mm, "end": v(15, -108) * mm});
            skLineSegment(sketch, "E89.MirrorCS", {"start": v(-15, -120) * mm, "end": v(-15, -108) * mm});
            skLineSegment(sketch, "E90.MirrorCS", {"start": v(0, -120) * mm, "end": v(0, -90) * mm, "construction": true});
            skLineSegment(sketch, "E91.MirrorCS", {"start": v(15, -108) * mm, "end": v(33, -90) * mm});
            skLineSegment(sketch, "E92.MirrorCS", {"start": v(-33, -90) * mm, "end": v(33, -90) * mm});
            skLineSegment(sketch, "E93.MirrorCS", {"start": v(-15, -108) * mm, "end": v(-33, -90) * mm});
            skArc(sketch, "E94.MirrorCS", {"start": v(15, -120) * mm, "mid": v(0, -135) * mm, "end": v(-15, -120) * mm});
            skCircle(sketch, "E95.MirrorC", {"center": v(0, -120) * mm, "radius": 6 * mm});
            skSolve(sketch);
        }
        {
            var Q0;
            Q0=makeQuery(id+"F16.imprint","IMPRINT",FACE,{"disambiguationData":[TD([[makeQuery(id+"F16.imprint","IMPRINT",EDGE,{"derivedFrom":sQuery(id+"F16.wireOp",EDGE,"E79")}),-1.0]])]});
            var Q1;
            Q1=makeQuery(id+"F16.imprint","IMPRINT",FACE,{"disambiguationData":[TD([[makeQuery(id+"F16.imprint","IMPRINT",EDGE,{"derivedFrom":sQuery(id+"F16.wireOp",EDGE,"E88.MirrorCS")}),1.0]])]});
            var Q2;
            {var subQ5=sQuery(id+"F16.wireOp",EDGE,"E86");Q2=makeQuery(id+"F16.imprint","IMPRINT",FACE,{"disambiguationData":[TD([[makeQuery(id+"F16.imprint","IMPRINT",EDGE,{"derivedFrom":subQ5}),-1.0]])]});}
            var Q3;
            Q3=makeQuery(id+"F2.opExtrude","CAP_FACE",FACE,{"disambiguationData":[OSD([sQuery(id+"F0.wireOp",EDGE,"E12"),sQuery(id+"F0.wireOp",EDGE,"E13"),sQuery(id+"F0.wireOp",EDGE,"E14"),sQuery(id+"F0.wireOp",EDGE,"E15"),sQuery(id+"F0.wireOp",EDGE,"E17.filletArc"),sQuery(id+"F0.wireOp",EDGE,"E18.filletArc"),sQuery(id+"F0.wireOp",EDGE,"E19.filletArc"),sQuery(id+"F0.wireOp",EDGE,"E20.filletArc"),sQuery(id+"F0.wireOp",EDGE,"E25.0"),sQuery(id+"F0.wireOp",EDGE,"E25.1"),sQuery(id+"F0.wireOp",EDGE,"E25.2"),sQuery(id+"F0.wireOp",EDGE,"E25.3"),sQuery(id+"F0.wireOp",EDGE,"E25.4"),sQuery(id+"F0.wireOp",EDGE,"E25.5"),sQuery(id+"F0.wireOp",EDGE,"E25.6"),sQuery(id+"F0.wireOp",EDGE,"E25.7")])],"isStart":false});
            extrude(context, id + "F17", {"entities" : qUnion([Q0, Q1, Q2]), "endBound" : BoundingType.UP_TO_SURFACE, "endBoundEntityFace" : qUnion([Q3]), "depth" : 25 * mm});
        }
    });
